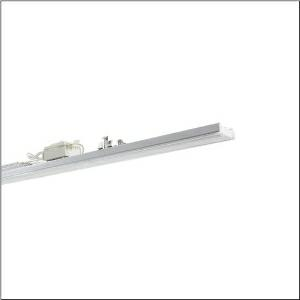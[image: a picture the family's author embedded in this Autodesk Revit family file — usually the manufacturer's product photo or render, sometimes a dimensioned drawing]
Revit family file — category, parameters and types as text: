
# Revit family: licross_r__11_recessed_mo_51te19dv4e5g_9f74
name_source: partatom
category: Lighting Fixtures
units: mm (PartAtom-declared; Revit-internal decimal feet)

## family parameters
Cut with Voids When Loaded = No
Host = Face
Light Source = No
Part Type = Normal
Room Calculation Point = No
Round Connector Dimension = Use Diameter
Shared = No

## types (1)
- --- (1 x LED, 14720 lm, 84.1 W, 4000K)
    Apparent Load = 84 VA
    CIE Flux Codes = 55 90 98 100 100
    Color Rendering = 80
    Color Temperature = 4000K
    Default Elevation = 1800 mm
    Description = Licross® 11 Recessed MO, luminaire insert, of sheet steel, galvanised, coil coated, white, length: 2.250mm, width: 66mm, height: 67mm, LED rated luminous flux: 14.720lm, light colour: 840, control gear: DALI 2, with plug, 5-pole, with phase selection, mains connection: 220..240V, AC, 50/60Hz, rated input power: 84W, halogen-free wiring, primary light control with lens, of plastic, primary optical cover: cover, of PMMA, light emission: direct distribution, primary light characteristic: double asymmetric, protection rating (complete): IP54, insulation class (complete): insulation class I (protective earthing), certification: CE, ENEC, VDE, UKCA, protection symbol: D if used in an environment with non-conductive dust loads with corresponding accessories, impact resistance: IK06, permissible ambient temperature for indoor applications: -25..+35°C, corresponds to IFS (International Featured Standards) requirements for safety and quality in the food industry, reducing of maximum allowable ambient temperature of 5°C with ceiling mounting, LABS conformity tested according to VDMA 24364:2018-05, packaging unit: 1 piece
    Height = 58 mm
    Lamp = 1 x LED
    Lamp Light Flux = 14720 lm
    Lamp Power = 84.1 W
    Lamp count = 1
    Length = 2250 mm
    Luminous efficacy = 175 lm/W
    Manufacturer = Siteco
    ModVariant = No
    Model = 51TE19DV4E5G
    Mounting Place = Ceiling
    Mounting Type = Pendant
    Number of Poles = 1
    OnlyDefault = Yes
    Power Factor = 1
    Product Name = Licross® 11 Recessed MO
    Product group = luminaire insert
    ProductGroupID = 902
    Protection Class = Protection class I
    Protection Degree = IP 54
    RLX_Detail_Level = 1
    RLX_Emergency_Light_Flux = 0 lm
    RLX_Emergency_Type = 0
    RLX_Emergency_Type_DB = No
    RlxData = <blob elided: 29717 chars, md5=d2978f7a>
    Socket = socket
    Standby Power = 0 W
    System Light Flux = 14720 lm
    System Power = 84 W
    Type Comments = factory setting: luminous flux: 100 % | dim-lin: 254 | 378 mA
    Type Image = l_1296930.jpg
    URL = http://relux.com
    VarID = @adj_100720
    Voltage = 0 V
    Weight = 0.00 kg
    Width = 66 mm

## geometry (parser evidence)
native form markers: Blend x4, Sweep x9
no freeform markers — native parametric forms only
